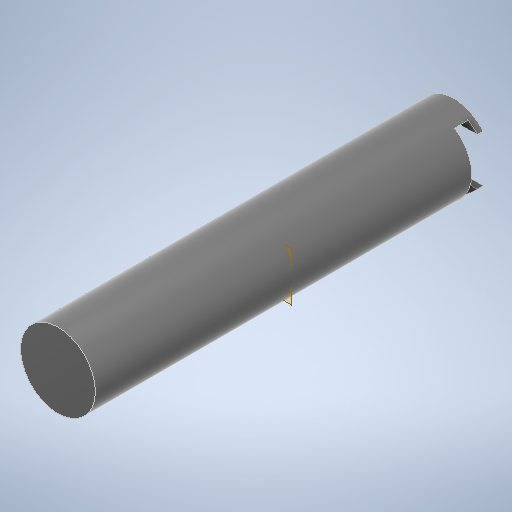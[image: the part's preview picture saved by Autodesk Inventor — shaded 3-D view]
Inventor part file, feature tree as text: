
AUTODESK INVENTOR PART (.ipt)
format: ipt  version: 2025.1 (Build 291241020, 241B)  size: 437,248 bytes
history: native  units: mm
features: extrude x6, sketch x6, plane x1, mirror x1
ambient origin geometry x8: Origin, YZ Plane, XZ Plane, XY Plane, X Axis, Y Axis, Z Axis, Center Point
bodies: Solid1 (feature_tree)
feature tree (14):
  extrude  "Extrusion1"  Depth=32.0mm
  plane  "Work Plane1"
  extrude  "Extrusion2"  Depth=3.0mm TaperAngle=0.0deg
  mirror  "Mirror1"
  extrude  "Extrusion5"  Depth=10.0mm TaperAngle=0.0deg
  extrude  "Extrusion6"  Depth=7.0mm
  extrude  "Extrusion7"  Depth=20.5mm
  extrude  "Extrusion8"  [1 undecoded]
  sketch  "Sketch1"  dims[d0=32.0mm d1=38.0mm]
  sketch  "Sketch2"  dims[d2=195.0mm d3=0.0mm d4=3.0mm d5=0.0mm]
  sketch  "Sketch5"  dims[d12=24.0mm d13=10.0mm d14=0.0mm]
  sketch  "Sketch6"  dims[d15=0.0mm d16=0.0mm d17=7.0mm]
  sketch  "Sketch7"  dims[d18=0.0mm d19=0.0mm d20=20.5mm]
  sketch  "Sketch8"  dims[d21=5.0mm d22=0.0mm]
note: 1 required parameter value undecoded (feature->parameter linkage not recoverable at this tier; creation-order binding heuristic only, values carry confidence <= 0.55)
